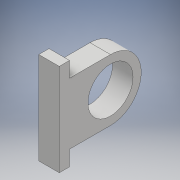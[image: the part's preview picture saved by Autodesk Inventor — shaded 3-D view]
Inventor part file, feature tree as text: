
AUTODESK INVENTOR PART (.ipt)
format: ipt  version: 2017 (Build 210142000, 142)  size: 129,024 bytes
history: native  units: mm
features: extrude x1, sketch x1
ambient origin geometry x8: Origin, YZ Plane, XZ Plane, XY Plane, X Axis, Y Axis, Z Axis, Center Point
bodies: Solid1 (feature_tree)
feature tree (2):
  extrude  "Extrusion1"  Depth=7.5mm
  sketch  "Sketch1"  dims[d0=22.0mm d1=27.5mm d2=25.0mm d3=180.0deg d4=20.0mm d7=5.0mm d8=5.0mm d9=5.0mm d10=5.0mm d11=30.0mm d12=10.0mm d13=0.0mm d14=5.0mm d15=7.5mm d16=5.0mm d17=7.5mm]
